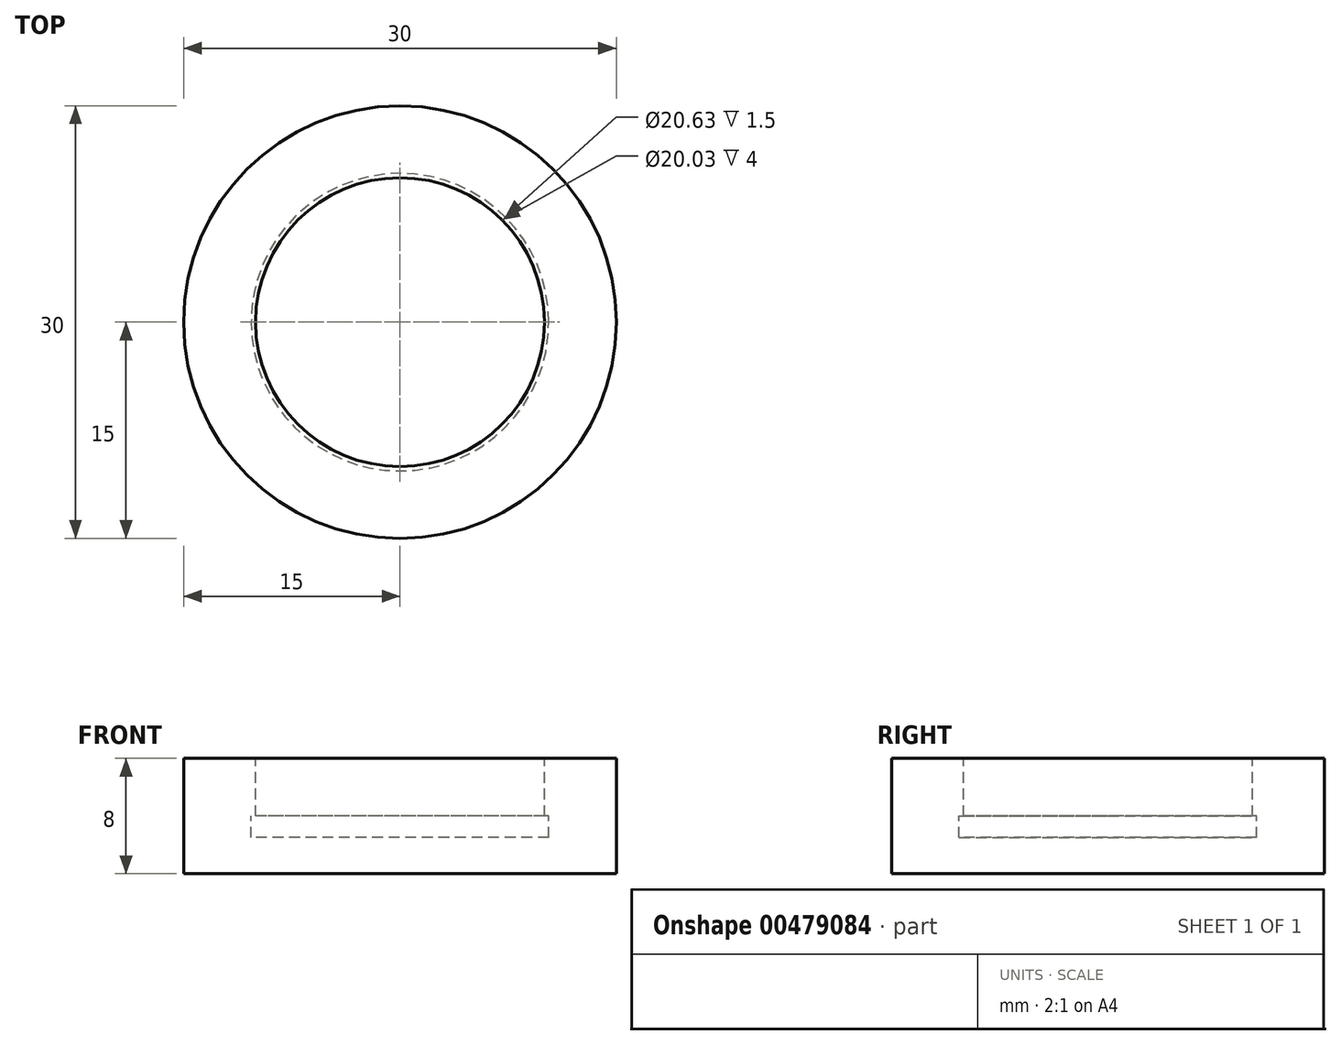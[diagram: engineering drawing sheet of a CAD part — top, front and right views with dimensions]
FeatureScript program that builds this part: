
annotation { "Feature Type Name" : "Feature", "Feature Type Description" : "" }
export const myFeature = defineFeature(function(context is Context, id is Id, definition is map)
    precondition{}
    {
        {
            var Q0;
            Q0=qCreatedBy(makeId("Front.planeOp"),FACE);
            var sketch = newSketch(context, id + "F0", { "sketchPlane" : qUnion([Q0])});
            skLineSegment(sketch, "E0", {"start": v(0, 0) * mm, "end": v(-15, 0) * mm});
            skLineSegment(sketch, "E1", {"start": v(-15, 0) * mm, "end": v(-15, 8) * mm});
            skLineSegment(sketch, "E2", {"start": v(-15, 8) * mm, "end": v(-10.02, 8) * mm});
            skLineSegment(sketch, "E3", {"start": v(-10.02, 8) * mm, "end": v(-10.02, 4) * mm});
            skLineSegment(sketch, "E4", {"start": v(-10.02, 4) * mm, "end": v(-10.32, 4) * mm});
            skLineSegment(sketch, "E5", {"start": v(-10.32, 4) * mm, "end": v(-10.32, 2.5) * mm});
            skLineSegment(sketch, "E6", {"start": v(-10.32, 2.5) * mm, "end": v(0, 2.5) * mm});
            skLineSegment(sketch, "E7", {"start": v(0, 2.5) * mm, "end": v(0, 0) * mm});
            skSolve(sketch);
        }
        {
            var Q0;
            Q0=makeQuery(id+"F0.imprint","IMPRINT",FACE,{"disambiguationData":[TD([[makeQuery(id+"F0.imprint","IMPRINT",EDGE,{"derivedFrom":sQuery(id+"F0.wireOp",EDGE,"E0")}),-1.0]])]});
            var Q1;
            Q1=sQuery(id+"F0.wireOp",EDGE,"E7");
            revolve(context, id + "F1", {"entities" : qUnion([Q0]), "axis" : qUnion([Q1]), "revolveType" : RevolveType.FULL});
        }
    });
